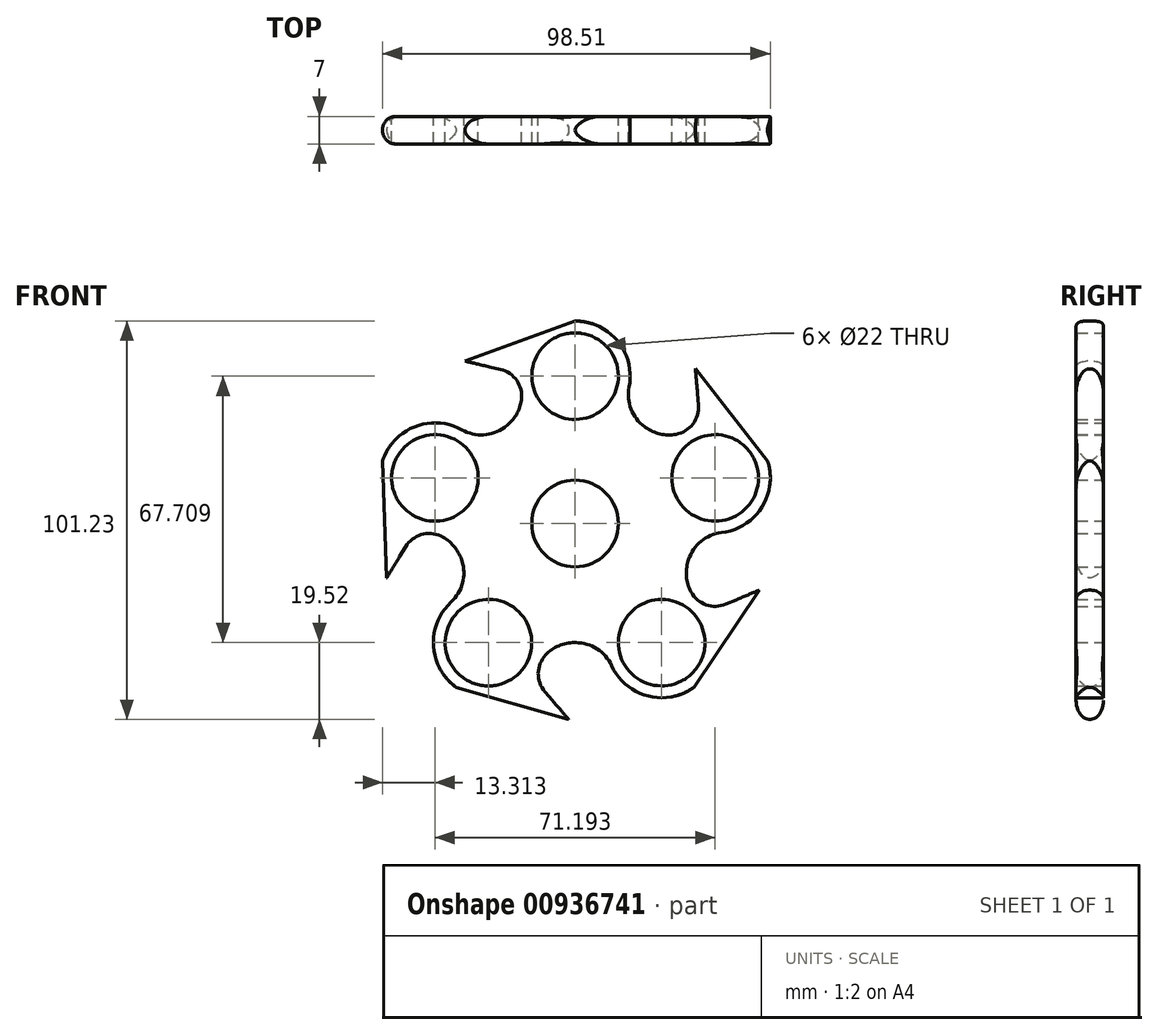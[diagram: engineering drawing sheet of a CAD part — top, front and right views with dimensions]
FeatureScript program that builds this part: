
annotation { "Feature Type Name" : "Feature", "Feature Type Description" : "" }
export const myFeature = defineFeature(function(context is Context, id is Id, definition is map)
    precondition{}
    {
        {
            var Q0;
            Q0=qCreatedBy(makeId("Front.planeOp"),FACE);
            var sketch = newSketch(context, id + "F0", { "sketchPlane" : qUnion([Q0])});
            skCircle(sketch, "E0", {"center": v(0, 0) * mm, "radius": 11 * mm});
            skArc(sketch, "E1.cCircle", {"start": v(25.6, 16.17) * mm, "mid": v(0, 30.28) * mm, "end": v(-25.6, 16.17) * mm, "construction": true});
            skLineSegment(sketch, "E1.0", {"start": v(11, -30.28) * mm, "end": v(-11, -30.28) * mm});
            skLineSegment(sketch, "E1.1", {"start": v(-25.4, -19.82) * mm, "end": v(-32.2, 1.1) * mm});
            skLineSegment(sketch, "E1.2", {"start": v(-26.7, 18.03) * mm, "end": v(0, 37.43) * mm});
            skLineSegment(sketch, "E1.3", {"start": v(0, 37.43) * mm, "end": v(26.7, 18.03) * mm});
            skLineSegment(sketch, "E1.4", {"start": v(32.2, 1.1) * mm, "end": v(25.4, -19.82) * mm});
            skPoint(sketch, "E1.0.midPoint", {"position": v(0, -30.28) * mm});
            skCircle(sketch, "E2", {"center": v(35.6, 11.57) * mm, "radius": 11 * mm});
            skCircle(sketch, "E3", {"center": v(35.6, 11.57) * mm, "radius": 14 * mm});
            skCircle(sketch, "E4", {"center": v(0, 37.43) * mm, "radius": 14 * mm});
            skCircle(sketch, "E5", {"center": v(0, 37.43) * mm, "radius": 11 * mm});
            skCircle(sketch, "E6", {"center": v(-35.6, 11.57) * mm, "radius": 14 * mm});
            skCircle(sketch, "E7", {"center": v(-35.6, 11.57) * mm, "radius": 11 * mm});
            skCircle(sketch, "E8", {"center": v(-22, -30.28) * mm, "radius": 14 * mm});
            skCircle(sketch, "E9", {"center": v(-22, -30.28) * mm, "radius": 11 * mm});
            skCircle(sketch, "E10", {"center": v(22, -30.28) * mm, "radius": 14 * mm});
            skCircle(sketch, "E11", {"center": v(22, -30.28) * mm, "radius": 11 * mm});
            skArc(sketch, "E12.trimOffspring", {"start": v(23.29, -19.36) * mm, "mid": v(28.8, -9.36) * mm, "end": v(30.22, 1.97) * mm, "construction": true});
            skArc(sketch, "E13.trimOffspring", {"start": v(-11.21, -28.13) * mm, "mid": v(0, -30.28) * mm, "end": v(11.21, -28.13) * mm, "construction": true});
            skArc(sketch, "E14.trimOffspring", {"start": v(-30.22, 1.97) * mm, "mid": v(-28.8, -9.36) * mm, "end": v(-23.29, -19.36) * mm, "construction": true});
            skLineSegment(sketch, "E15", {"start": v(0, 51.43) * mm, "end": v(-27.97, 41.24) * mm});
            skLineSegment(sketch, "E16", {"start": v(-27.97, 41.24) * mm, "end": v(-14, 37.95) * mm});
            skLineSegment(sketch, "E17.1.0", {"start": v(-48.91, 15.9) * mm, "end": v(-47.86, -13.86) * mm});
            skLineSegment(sketch, "E17.1.1", {"start": v(-47.86, -13.86) * mm, "end": v(-40.42, -1.58) * mm});
            skLineSegment(sketch, "E17.2.0", {"start": v(-30.23, -41.6) * mm, "end": v(-1.61, -49.8) * mm});
            skLineSegment(sketch, "E17.2.1", {"start": v(-1.61, -49.8) * mm, "end": v(-11, -38.93) * mm});
            skLineSegment(sketch, "E17.3.0", {"start": v(30.23, -41.6) * mm, "end": v(46.87, -16.92) * mm});
            skLineSegment(sketch, "E17.3.1", {"start": v(46.87, -16.92) * mm, "end": v(33.63, -22.48) * mm});
            skLineSegment(sketch, "E17.4.0", {"start": v(48.91, 15.9) * mm, "end": v(30.58, 39.34) * mm});
            skLineSegment(sketch, "E17.4.1", {"start": v(30.58, 39.34) * mm, "end": v(31.77, 25.03) * mm});
            skSolve(sketch);
        }
        {
            var Q0;
            {var subQ0=sQuery(id+"F0.wireOp",EDGE,"E17.4.1");Q0=makeQuery(id+"F0.imprint","IMPRINT",FACE,{"disambiguationData":[TD([[makeQuery(id+"F0.imprint","IMPRINT",EDGE,{"derivedFrom":subQ0}),1.0]])]});}
            var Q1;
            {var subQ0=sQuery(id+"F0.wireOp",EDGE,"E16");Q1=makeQuery(id+"F0.imprint","IMPRINT",FACE,{"disambiguationData":[TD([[makeQuery(id+"F0.imprint","IMPRINT",EDGE,{"derivedFrom":subQ0}),1.0]])]});}
            var Q2;
            {var subQ0=sQuery(id+"F0.wireOp",EDGE,"E17.1.1");Q2=makeQuery(id+"F0.imprint","IMPRINT",FACE,{"disambiguationData":[TD([[makeQuery(id+"F0.imprint","IMPRINT",EDGE,{"derivedFrom":subQ0}),1.0]])]});}
            var Q3;
            {var subQ0=sQuery(id+"F0.wireOp",EDGE,"E17.2.1");Q3=makeQuery(id+"F0.imprint","IMPRINT",FACE,{"disambiguationData":[TD([[makeQuery(id+"F0.imprint","IMPRINT",EDGE,{"derivedFrom":subQ0}),1.0]])]});}
            var Q4;
            {var subQ0=sQuery(id+"F0.wireOp",EDGE,"E17.3.1");Q4=makeQuery(id+"F0.imprint","IMPRINT",FACE,{"disambiguationData":[TD([[makeQuery(id+"F0.imprint","IMPRINT",EDGE,{"derivedFrom":subQ0}),1.0]])]});}
            var Q5;
            {var subQ0=sQuery(id+"F0.wireOp",EDGE,"E11");var subQ1=sQuery(id+"F0.wireOp",EDGE,"E1.0");var subQ2=makeQuery(id+"F0.imprint","INTERSECT",VERTEX,{"derivedFrom":[subQ1,subQ0]});Q5=makeQuery(id+"F0.imprint","IMPRINT",FACE,{"disambiguationData":[TD([[makeQuery(id+"F0.imprint","IMPRINT",EDGE,{"disambiguationData":[TD([[subQ2,-1.0]])],"derivedFrom":subQ1}),-1.0]])]});}
            var Q6;
            {var subQ0=sQuery(id+"F0.wireOp",EDGE,"E9");var subQ1=sQuery(id+"F0.wireOp",EDGE,"E1.0");var subQ2=makeQuery(id+"F0.imprint","INTERSECT",VERTEX,{"derivedFrom":[subQ1,subQ0]});Q6=makeQuery(id+"F0.imprint","IMPRINT",FACE,{"disambiguationData":[TD([[makeQuery(id+"F0.imprint","IMPRINT",EDGE,{"disambiguationData":[TD([[subQ2,1.0]])],"derivedFrom":subQ1}),-1.0]])]});}
            var Q7;
            {var subQ0=sQuery(id+"F0.wireOp",EDGE,"E7");var subQ1=sQuery(id+"F0.wireOp",EDGE,"E1.1");var subQ2=makeQuery(id+"F0.imprint","INTERSECT",VERTEX,{"derivedFrom":[subQ1,subQ0]});Q7=makeQuery(id+"F0.imprint","IMPRINT",FACE,{"disambiguationData":[TD([[makeQuery(id+"F0.imprint","IMPRINT",EDGE,{"disambiguationData":[TD([[subQ2,1.0]])],"derivedFrom":subQ1}),-1.0]])]});}
            var Q8;
            {var subQ0=sQuery(id+"F0.wireOp",EDGE,"E4");var subQ1=sQuery(id+"F0.wireOp",EDGE,"E1.2");var subQ2=makeQuery(id+"F0.imprint","INTERSECT",VERTEX,{"derivedFrom":[subQ1,subQ0]});Q8=makeQuery(id+"F0.imprint","IMPRINT",FACE,{"disambiguationData":[TD([[makeQuery(id+"F0.imprint","IMPRINT",EDGE,{"disambiguationData":[TD([[subQ2,-1.0]])],"derivedFrom":subQ1}),-1.0]])]});}
            var Q9;
            {var subQ0=sQuery(id+"F0.wireOp",EDGE,"E2");var subQ1=sQuery(id+"F0.wireOp",EDGE,"E1.3");var subQ2=makeQuery(id+"F0.imprint","INTERSECT",VERTEX,{"derivedFrom":[subQ1,subQ0]});Q9=makeQuery(id+"F0.imprint","IMPRINT",FACE,{"disambiguationData":[TD([[makeQuery(id+"F0.imprint","IMPRINT",EDGE,{"disambiguationData":[TD([[subQ2,1.0]])],"derivedFrom":subQ1}),-1.0]])]});}
            var Q10;
            {var subQ3=sQuery(id+"F0.wireOp",EDGE,"E1.0");var subQ5=sQuery(id+"F0.wireOp",EDGE,"E11");var subQ11=makeQuery(id+"F0.imprint","INTERSECT",VERTEX,{"derivedFrom":[subQ3,subQ5]});Q10=makeQuery(id+"F0.imprint","IMPRINT",FACE,{"disambiguationData":[TD([[makeQuery(id+"F0.imprint","IMPRINT",EDGE,{"disambiguationData":[TD([[subQ11,-1.0]])],"derivedFrom":subQ3}),1.0]])]});}
            var Q11;
            {var subQ7=sQuery(id+"F0.wireOp",EDGE,"E9");var subQ9=sQuery(id+"F0.wireOp",EDGE,"E1.0");var subQ10=makeQuery(id+"F0.imprint","INTERSECT",VERTEX,{"derivedFrom":[subQ9,subQ7]});Q11=makeQuery(id+"F0.imprint","IMPRINT",FACE,{"disambiguationData":[TD([[makeQuery(id+"F0.imprint","IMPRINT",EDGE,{"disambiguationData":[TD([[subQ10,1.0]])],"derivedFrom":subQ9}),1.0]])]});}
            var Q12;
            {var subQ7=sQuery(id+"F0.wireOp",EDGE,"E7");var subQ9=sQuery(id+"F0.wireOp",EDGE,"E1.1");var subQ10=makeQuery(id+"F0.imprint","INTERSECT",VERTEX,{"derivedFrom":[subQ9,subQ7]});Q12=makeQuery(id+"F0.imprint","IMPRINT",FACE,{"disambiguationData":[TD([[makeQuery(id+"F0.imprint","IMPRINT",EDGE,{"disambiguationData":[TD([[subQ10,1.0]])],"derivedFrom":subQ9}),1.0]])]});}
            var Q13;
            {var subQ0=sQuery(id+"F0.wireOp",EDGE,"E4");var subQ4=sQuery(id+"F0.wireOp",EDGE,"E1.2");var subQ5=makeQuery(id+"F0.imprint","INTERSECT",VERTEX,{"derivedFrom":[subQ4,subQ0]});Q13=makeQuery(id+"F0.imprint","IMPRINT",FACE,{"disambiguationData":[TD([[makeQuery(id+"F0.imprint","IMPRINT",EDGE,{"disambiguationData":[TD([[subQ5,-1.0]])],"derivedFrom":subQ4}),1.0]])]});}
            var Q14;
            {var subQ5=sQuery(id+"F0.wireOp",EDGE,"E2");var subQ9=sQuery(id+"F0.wireOp",EDGE,"E1.3");var subQ10=makeQuery(id+"F0.imprint","INTERSECT",VERTEX,{"derivedFrom":[subQ9,subQ5]});Q14=makeQuery(id+"F0.imprint","IMPRINT",FACE,{"disambiguationData":[TD([[makeQuery(id+"F0.imprint","IMPRINT",EDGE,{"disambiguationData":[TD([[subQ10,1.0]])],"derivedFrom":subQ9}),1.0]])]});}
            var Q15;
            Q15=makeQuery(id+"F0.imprint","IMPRINT",FACE,{"disambiguationData":[TD([[makeQuery(id+"F0.imprint","IMPRINT",EDGE,{"derivedFrom":sQuery(id+"F0.wireOp",EDGE,"E0")}),-1.0]])]});
            extrude(context, id + "F1", {"entities" : qUnion([Q0, Q1, Q2, Q3, Q4, Q5, Q6, Q7, Q8, Q9, Q10, Q11, Q12, Q13, Q14, Q15]), "depth" : 7 * mm, "offsetDistance" : 25 * mm});
        }
        {
            var Q0;
            Q0=makeQuery(id+"F1.opExtrude","SWEPT_EDGE",EDGE,{"disambiguationData":[OSD([sQuery(id+"F0.wireOp",EDGE,"E1.0"),sQuery(id+"F0.wireOp",EDGE,"E10")])]});
            var Q1;
            Q1=makeQuery(id+"F1.opExtrude","SWEPT_EDGE",EDGE,{"disambiguationData":[OSD([sQuery(id+"F0.wireOp",EDGE,"E1.0"),sQuery(id+"F0.wireOp",EDGE,"E8")])]});
            var Q2;
            Q2=makeQuery(id+"F1.opExtrude","SWEPT_EDGE",EDGE,{"disambiguationData":[OSD([sQuery(id+"F0.wireOp",EDGE,"E1.1"),sQuery(id+"F0.wireOp",EDGE,"E6")])]});
            var Q3;
            Q3=makeQuery(id+"F1.opExtrude","SWEPT_EDGE",EDGE,{"disambiguationData":[OSD([sQuery(id+"F0.wireOp",EDGE,"E1.1"),sQuery(id+"F0.wireOp",EDGE,"E8")])]});
            var Q4;
            Q4=makeQuery(id+"F1.opExtrude","SWEPT_EDGE",EDGE,{"disambiguationData":[OSD([sQuery(id+"F0.wireOp",EDGE,"E1.2"),sQuery(id+"F0.wireOp",EDGE,"E4")])]});
            var Q5;
            Q5=makeQuery(id+"F1.opExtrude","SWEPT_EDGE",EDGE,{"disambiguationData":[OSD([sQuery(id+"F0.wireOp",EDGE,"E1.2"),sQuery(id+"F0.wireOp",EDGE,"E6")])]});
            var Q6;
            Q6=makeQuery(id+"F1.opExtrude","SWEPT_EDGE",EDGE,{"disambiguationData":[OSD([sQuery(id+"F0.wireOp",EDGE,"E1.4"),sQuery(id+"F0.wireOp",EDGE,"E10")])]});
            var Q7;
            Q7=makeQuery(id+"F1.opExtrude","SWEPT_EDGE",EDGE,{"disambiguationData":[OSD([sQuery(id+"F0.wireOp",EDGE,"E1.4"),sQuery(id+"F0.wireOp",EDGE,"E3")])]});
            var Q8;
            Q8=makeQuery(id+"F1.opExtrude","SWEPT_EDGE",EDGE,{"disambiguationData":[OSD([sQuery(id+"F0.wireOp",EDGE,"E1.3"),sQuery(id+"F0.wireOp",EDGE,"E4")])]});
            var Q9;
            Q9=makeQuery(id+"F1.opExtrude","SWEPT_EDGE",EDGE,{"disambiguationData":[OSD([sQuery(id+"F0.wireOp",EDGE,"E1.3"),sQuery(id+"F0.wireOp",EDGE,"E3")])]});
            fillet(context, id + "F2", {"entities" : qUnion([Q0, Q1, Q2, Q3, Q4, Q5, Q6, Q7, Q8, Q9]), "radius" : 10 * mm, "tangentPropagation" : true, "allowEdgeOverflow" : false});
        }
        {
            var Q0;
            Q0=makeQuery(id+"F1.opExtrude","SWEPT_EDGE",EDGE,{"disambiguationData":[OSD([sQuery(id+"F0.wireOp",EDGE,"E6"),sQuery(id+"F0.wireOp",EDGE,"E17.1.1")])]});
            var Q1;
            Q1=makeQuery(id+"F1.opExtrude","SWEPT_EDGE",EDGE,{"disambiguationData":[OSD([sQuery(id+"F0.wireOp",EDGE,"E8"),sQuery(id+"F0.wireOp",EDGE,"E17.2.1")])]});
            var Q2;
            Q2=makeQuery(id+"F1.opExtrude","SWEPT_EDGE",EDGE,{"disambiguationData":[OSD([sQuery(id+"F0.wireOp",EDGE,"E10"),sQuery(id+"F0.wireOp",EDGE,"E17.3.1")])]});
            var Q3;
            Q3=makeQuery(id+"F1.opExtrude","SWEPT_EDGE",EDGE,{"disambiguationData":[OSD([sQuery(id+"F0.wireOp",EDGE,"E3"),sQuery(id+"F0.wireOp",EDGE,"E17.4.1")])]});
            var Q4;
            Q4=makeQuery(id+"F1.opExtrude","SWEPT_EDGE",EDGE,{"disambiguationData":[OSD([sQuery(id+"F0.wireOp",EDGE,"E4"),sQuery(id+"F0.wireOp",EDGE,"E16")])]});
            fillet(context, id + "F3", {"entities" : qUnion([Q0, Q1, Q2, Q3, Q4]), "radius" : 7 * mm, "tangentPropagation" : true, "allowEdgeOverflow" : false});
        }
        {
            var Q0;
            Q0=makeQuery(id+"F1.opExtrude","CAP_EDGE",EDGE,{"disambiguationData":[OSD([sQuery(id+"F0.wireOp",EDGE,"E17.3.0")])],"isStart":false});
            var Q1;
            Q1=makeQuery(id+"F1.opExtrude","CAP_EDGE",EDGE,{"disambiguationData":[OSD([sQuery(id+"F0.wireOp",EDGE,"E17.3.0")])],"isStart":true});
            var Q2;
            {var subQ0=sQuery(id+"F0.wireOp",EDGE,"E10");Q2=makeQuery(id+"F1.opExtrude","CAP_EDGE",EDGE,{"disambiguationData":[OSD([subQ0]),TDD([makeQuery(id+"F0.imprint","IMPRINT",EDGE,{"disambiguationData":[TD([[makeQuery(id+"F0.imprint","INTERSECT",VERTEX,{"disambiguationData":[OD(0.0)],"derivedFrom":[subQ0,sQuery(id+"F0.wireOp",EDGE,"E17.3.0")]}),1.0]])],"derivedFrom":subQ0})])],"isStart":false});}
            var Q3;
            {var subQ0=sQuery(id+"F0.wireOp",EDGE,"E10");Q3=makeQuery(id+"F1.opExtrude","CAP_EDGE",EDGE,{"disambiguationData":[OSD([subQ0]),TDD([makeQuery(id+"F0.imprint","IMPRINT",EDGE,{"disambiguationData":[TD([[makeQuery(id+"F0.imprint","INTERSECT",VERTEX,{"disambiguationData":[OD(0.0)],"derivedFrom":[subQ0,sQuery(id+"F0.wireOp",EDGE,"E17.3.0")]}),1.0]])],"derivedFrom":subQ0})])],"isStart":true});}
            var Q4;
            Q4=makeQuery(id+"F1.opExtrude","CAP_EDGE",EDGE,{"disambiguationData":[OSD([sQuery(id+"F0.wireOp",EDGE,"E17.2.0")])],"isStart":false});
            var Q5;
            Q5=makeQuery(id+"F1.opExtrude","CAP_EDGE",EDGE,{"disambiguationData":[OSD([sQuery(id+"F0.wireOp",EDGE,"E17.2.0")])],"isStart":true});
            var Q6;
            {var subQ0=sQuery(id+"F0.wireOp",EDGE,"E8");Q6=makeQuery(id+"F1.opExtrude","CAP_EDGE",EDGE,{"disambiguationData":[OSD([subQ0]),TDD([makeQuery(id+"F0.imprint","IMPRINT",EDGE,{"disambiguationData":[TD([[makeQuery(id+"F0.imprint","INTERSECT",VERTEX,{"disambiguationData":[OD(0.0)],"derivedFrom":[subQ0,sQuery(id+"F0.wireOp",EDGE,"E17.2.0")]}),1.0]])],"derivedFrom":subQ0})])],"isStart":true});}
            var Q7;
            {var subQ0=sQuery(id+"F0.wireOp",EDGE,"E8");Q7=makeQuery(id+"F1.opExtrude","CAP_EDGE",EDGE,{"disambiguationData":[OSD([subQ0]),TDD([makeQuery(id+"F0.imprint","IMPRINT",EDGE,{"disambiguationData":[TD([[makeQuery(id+"F0.imprint","INTERSECT",VERTEX,{"disambiguationData":[OD(0.0)],"derivedFrom":[subQ0,sQuery(id+"F0.wireOp",EDGE,"E17.2.0")]}),1.0]])],"derivedFrom":subQ0})])],"isStart":false});}
            var Q8;
            Q8=makeQuery(id+"F1.opExtrude","CAP_EDGE",EDGE,{"disambiguationData":[OSD([sQuery(id+"F0.wireOp",EDGE,"E17.1.0")])],"isStart":true});
            var Q9;
            Q9=makeQuery(id+"F1.opExtrude","CAP_EDGE",EDGE,{"disambiguationData":[OSD([sQuery(id+"F0.wireOp",EDGE,"E17.1.0")])],"isStart":false});
            var Q10;
            {var subQ0=sQuery(id+"F0.wireOp",EDGE,"E6");Q10=makeQuery(id+"F1.opExtrude","CAP_EDGE",EDGE,{"disambiguationData":[OSD([subQ0]),TDD([makeQuery(id+"F0.imprint","IMPRINT",EDGE,{"disambiguationData":[TD([[makeQuery(id+"F0.imprint","INTERSECT",VERTEX,{"disambiguationData":[OD(0.0)],"derivedFrom":[subQ0,sQuery(id+"F0.wireOp",EDGE,"E17.1.0")]}),1.0]])],"derivedFrom":subQ0})])],"isStart":false});}
            var Q11;
            {var subQ0=sQuery(id+"F0.wireOp",EDGE,"E6");Q11=makeQuery(id+"F1.opExtrude","CAP_EDGE",EDGE,{"disambiguationData":[OSD([subQ0]),TDD([makeQuery(id+"F0.imprint","IMPRINT",EDGE,{"disambiguationData":[TD([[makeQuery(id+"F0.imprint","INTERSECT",VERTEX,{"disambiguationData":[OD(0.0)],"derivedFrom":[subQ0,sQuery(id+"F0.wireOp",EDGE,"E17.1.0")]}),1.0]])],"derivedFrom":subQ0})])],"isStart":true});}
            var Q12;
            Q12=makeQuery(id+"F1.opExtrude","CAP_EDGE",EDGE,{"disambiguationData":[OSD([sQuery(id+"F0.wireOp",EDGE,"E17.4.0")])],"isStart":true});
            var Q13;
            Q13=makeQuery(id+"F1.opExtrude","CAP_EDGE",EDGE,{"disambiguationData":[OSD([sQuery(id+"F0.wireOp",EDGE,"E17.4.0")])],"isStart":false});
            var Q14;
            {var subQ0=sQuery(id+"F0.wireOp",EDGE,"E3");Q14=makeQuery(id+"F1.opExtrude","CAP_EDGE",EDGE,{"disambiguationData":[OSD([subQ0]),TDD([makeQuery(id+"F0.imprint","IMPRINT",EDGE,{"disambiguationData":[TD([[makeQuery(id+"F0.imprint","INTERSECT",VERTEX,{"disambiguationData":[OD(0.0)],"derivedFrom":[subQ0,sQuery(id+"F0.wireOp",EDGE,"E17.4.0")]}),1.0]])],"derivedFrom":subQ0})])],"isStart":true});}
            var Q15;
            {var subQ0=sQuery(id+"F0.wireOp",EDGE,"E3");Q15=makeQuery(id+"F1.opExtrude","CAP_EDGE",EDGE,{"disambiguationData":[OSD([subQ0]),TDD([makeQuery(id+"F0.imprint","IMPRINT",EDGE,{"disambiguationData":[TD([[makeQuery(id+"F0.imprint","INTERSECT",VERTEX,{"disambiguationData":[OD(0.0)],"derivedFrom":[subQ0,sQuery(id+"F0.wireOp",EDGE,"E17.4.0")]}),1.0]])],"derivedFrom":subQ0})])],"isStart":false});}
            var Q16;
            Q16=makeQuery(id+"F1.opExtrude","CAP_EDGE",EDGE,{"disambiguationData":[OSD([sQuery(id+"F0.wireOp",EDGE,"E15")])],"isStart":true});
            var Q17;
            Q17=makeQuery(id+"F1.opExtrude","CAP_EDGE",EDGE,{"disambiguationData":[OSD([sQuery(id+"F0.wireOp",EDGE,"E15")])],"isStart":false});
            var Q18;
            {var subQ0=sQuery(id+"F0.wireOp",EDGE,"E4");Q18=makeQuery(id+"F1.opExtrude","CAP_EDGE",EDGE,{"disambiguationData":[OSD([subQ0]),TDD([makeQuery(id+"F0.imprint","IMPRINT",EDGE,{"disambiguationData":[TD([[makeQuery(id+"F0.imprint","INTERSECT",VERTEX,{"disambiguationData":[OD(0.0)],"derivedFrom":[subQ0,sQuery(id+"F0.wireOp",EDGE,"E15")]}),1.0]])],"derivedFrom":subQ0})])],"isStart":true});}
            var Q19;
            {var subQ0=sQuery(id+"F0.wireOp",EDGE,"E4");Q19=makeQuery(id+"F1.opExtrude","CAP_EDGE",EDGE,{"disambiguationData":[OSD([subQ0]),TDD([makeQuery(id+"F0.imprint","IMPRINT",EDGE,{"disambiguationData":[TD([[makeQuery(id+"F0.imprint","INTERSECT",VERTEX,{"disambiguationData":[OD(0.0)],"derivedFrom":[subQ0,sQuery(id+"F0.wireOp",EDGE,"E15")]}),1.0]])],"derivedFrom":subQ0})])],"isStart":false});}
            fillet(context, id + "F4", {"entities" : qUnion([Q0, Q1, Q2, Q3, Q4, Q5, Q6, Q7, Q8, Q9, Q10, Q11, Q12, Q13, Q14, Q15, Q16, Q17, Q18, Q19]), "radius" : 3.5 * mm, "tangentPropagation" : true, "allowEdgeOverflow" : false});
        }
    });
